# Revit family: HVAC_Fan-Assisted-Distributors_Neptronic_SKH4_MDU-1000
name_source: partatom
category: Mechanical Equipment
units: mm (PartAtom-declared; Revit-internal decimal feet)

## family parameters
Always vertical = No
Classification = None
Cut with Voids When Loaded = No
OmniClass Number = 23.33.27.15
Part Type = Normal
Room Calculation Point = No
Round Connector Dimension = Use Diameter
Shared = No
Work Plane-Based = Yes

## types (2) — shared parameters
CFM = 1000 CFM
Default Elevation = 0.00 in
Depth = 0.00 in
Description = Radial projection mist distributor
Diameter = 20.30 in
Frequency = 50 Hz
Height = 9.00 in
Length = 0.00 in
Manufacturer = Neptronic
Model Type = MDU
Mounting Type = Suspended
Nozzle Capacity = 60lb/h to 120lb/h
Number of Poles = 1
Number of Spray Nozzles = 9
Plumbing Connection Diameter = 0.70 in
Power Factor = 1
Product Material = Neptronic - Stainless steel
Product Page URL = https://www.neptronic.com
RLA = 1 A
URL = https://www.neptronic.com
Weight = 22.00 lb
Width = 0.00 in

## per-type parameters (varying)
| type | Apparent Load | Supply Voltage | Version | Voltage |
| SKH4-MDU-1000-A-9 | 168 VA | A | 0 | 120 V |
| SKH4-MDU-1000-C-9 | 120 VA | C | 1 | 240 V |

note: column(s) folded — value = type name in every type: Model

## geometry (parser evidence)
native form markers: Sweep x4
no freeform markers — native parametric forms only
